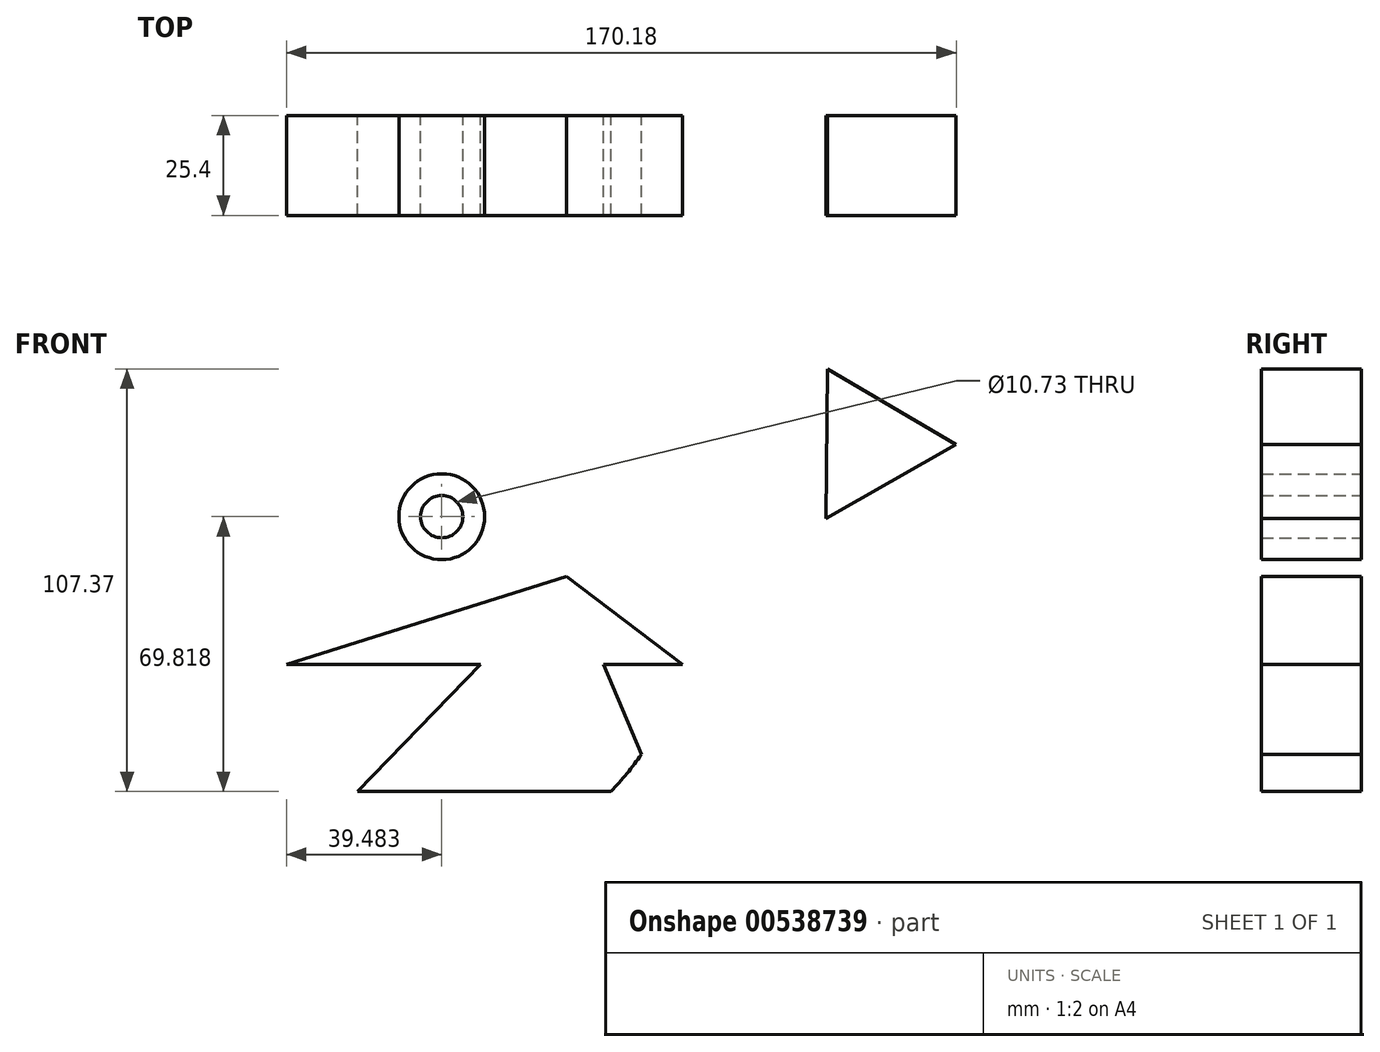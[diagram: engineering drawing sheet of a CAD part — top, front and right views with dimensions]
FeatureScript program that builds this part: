
annotation { "Feature Type Name" : "Feature", "Feature Type Description" : "" }
export const myFeature = defineFeature(function(context is Context, id is Id, definition is map)
    precondition{}
    {
        {
            var Q0;
            Q0=qCreatedBy(makeId("Front.planeOp"),FACE);
            var sketch = newSketch(context, id + "F0", { "sketchPlane" : qUnion([Q0])});
            skLineSegment(sketch, "E0", {"start": v(-23.05, 54.68) * mm, "end": v(-76.12, 0) * mm});
            skLineSegment(sketch, "E1", {"start": v(-23.05, 54.68) * mm, "end": v(-16.49, 39.12) * mm});
            skLineSegment(sketch, "E2", {"start": v(0, 0) * mm, "end": v(-76.12, 0) * mm});
            skLineSegment(sketch, "E3", {"start": v(-23.05, 54.68) * mm, "end": v(-94.2, 32.24) * mm});
            skLineSegment(sketch, "E4", {"start": v(-94.2, 32.24) * mm, "end": v(6.5, 32.24) * mm});
            skLineSegment(sketch, "E5", {"start": v(6.5, 32.24) * mm, "end": v(-23.05, 54.68) * mm});
            skCircle(sketch, "E6", {"center": v(-54.73, 69.82) * mm, "radius": 10.9 * mm});
            skCircle(sketch, "E7", {"center": v(-54.73, 69.82) * mm, "radius": 3.19 * mm});
            skCircle(sketch, "E8", {"center": v(-54.73, 69.82) * mm, "radius": 5.36 * mm});
            skArc(sketch, "E9", {"start": v(6.5, 32.24) * mm, "mid": v(-135.76, 68.48) * mm, "end": v(7.2, 35.12) * mm});
            skArc(sketch, "E10", {"start": v(6.5, 44.67) * mm, "mid": v(2.79, 54.7) * mm, "end": v(-7.82, 53.26) * mm});
            skCircle(sketch, "E11", {"center": v(-27.4, 80.48) * mm, "radius": 3.19 * mm});
            skLineSegment(sketch, "E12", {"start": v(-27.4, 83.67) * mm, "end": v(-17.87, 83.67) * mm});
            skLineSegment(sketch, "E13", {"start": v(-17.87, 64.63) * mm, "end": v(-17.87, 77.15) * mm});
            skLineSegment(sketch, "E14.trimOffspring", {"start": v(-13.59, 32.24) * mm, "end": v(0, 0) * mm});
            skArc(sketch, "E15.trimOffspring", {"start": v(-22.42, 55.33) * mm, "mid": v(-5.13, 67.75) * mm, "end": v(6.54, 49.95) * mm});
            skCircle(sketch, "E16.cCircle", {"center": v(54.03, 88.28) * mm, "radius": 10.97 * mm, "construction": true});
            skLineSegment(sketch, "E16.0", {"start": v(75.97, 88.1) * mm, "end": v(42.9, 69.37) * mm});
            skLineSegment(sketch, "E16.1", {"start": v(42.9, 69.37) * mm, "end": v(43.21, 107.37) * mm});
            skLineSegment(sketch, "E16.2", {"start": v(43.21, 107.37) * mm, "end": v(75.97, 88.1) * mm});
            skPoint(sketch, "E16.0.midPoint", {"position": v(59.44, 78.74) * mm});
            skSolve(sketch);
        }
        {
            var Q0;
            {var subQ0=sQuery(id+"F0.wireOp",EDGE,"E3");Q0=makeQuery(id+"F0.imprint","IMPRINT",FACE,{"disambiguationData":[TD([[makeQuery(id+"F0.imprint","IMPRINT",EDGE,{"derivedFrom":subQ0}),1.0]])]});}
            var Q1;
            {var subQ1=sQuery(id+"F0.wireOp",EDGE,"E2");var subQ5=sQuery(id+"F0.wireOp",EDGE,"E0");var subQ6=makeQuery(id+"F0.imprint","INTERSECT",VERTEX,{"derivedFrom":[subQ5,subQ1]});Q1=makeQuery(id+"F0.imprint","IMPRINT",FACE,{"disambiguationData":[TD([[makeQuery(id+"F0.imprint","IMPRINT",EDGE,{"disambiguationData":[TD([[subQ6,1.0]])],"derivedFrom":subQ5}),1.0]])]});}
            var Q2;
            {var subQ0=sQuery(id+"F0.wireOp",EDGE,"E5");Q2=makeQuery(id+"F0.imprint","IMPRINT",FACE,{"disambiguationData":[TD([[makeQuery(id+"F0.imprint","IMPRINT",EDGE,{"derivedFrom":subQ0}),1.0]])]});}
            var Q3;
            Q3=makeQuery(id+"F0.imprint","IMPRINT",FACE,{"disambiguationData":[TD([[makeQuery(id+"F0.imprint","IMPRINT",EDGE,{"derivedFrom":sQuery(id+"F0.wireOp",EDGE,"E6")}),1.0]])]});
            var Q4;
            Q4=makeQuery(id+"F0.imprint","IMPRINT",FACE,{"disambiguationData":[TD([[makeQuery(id+"F0.imprint","IMPRINT",EDGE,{"derivedFrom":sQuery(id+"F0.wireOp",EDGE,"E16.0")}),-1.0]])]});
            extrude(context, id + "F1", {"entities" : qUnion([Q0, Q1, Q2, Q3, Q4]), "depth" : 25.4 * mm, "offsetDistance" : 25.4 * mm});
        }
    });
